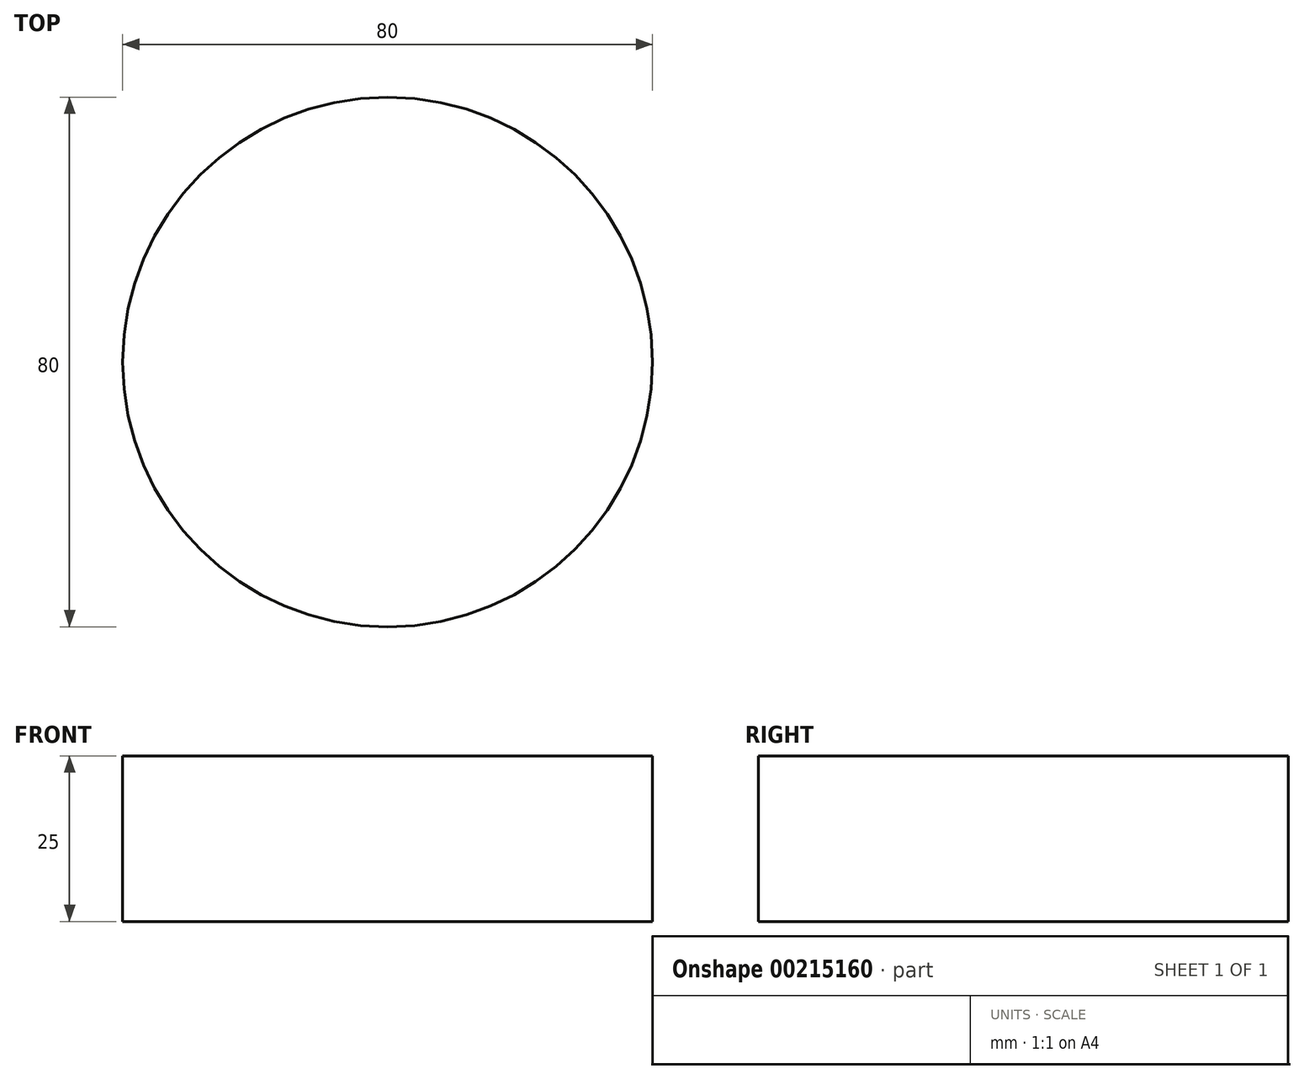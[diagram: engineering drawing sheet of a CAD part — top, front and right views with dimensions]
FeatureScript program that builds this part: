
annotation { "Feature Type Name" : "Feature", "Feature Type Description" : "" }
export const myFeature = defineFeature(function(context is Context, id is Id, definition is map)
    precondition{}
    {
        {
            var Q0;
            Q0=qCreatedBy(makeId("Top.planeOp"),FACE);
            var sketch = newSketch(context, id + "F0", { "sketchPlane" : qUnion([Q0])});
            skCircle(sketch, "E0", {"center": v(0, 0) * mm, "radius": 40 * mm});
            skSolve(sketch);
        }
        {
            var Q0;
            Q0=makeQuery(id+"F0.imprint","IMPRINT",FACE,{"disambiguationData":[TD([[makeQuery(id+"F0.imprint","IMPRINT",EDGE,{"derivedFrom":sQuery(id+"F0.wireOp",EDGE,"E0")}),1.0]])]});
            extrude(context, id + "F1", {"entities" : qUnion([Q0]), "depth" : 25 * mm});
        }
    });
